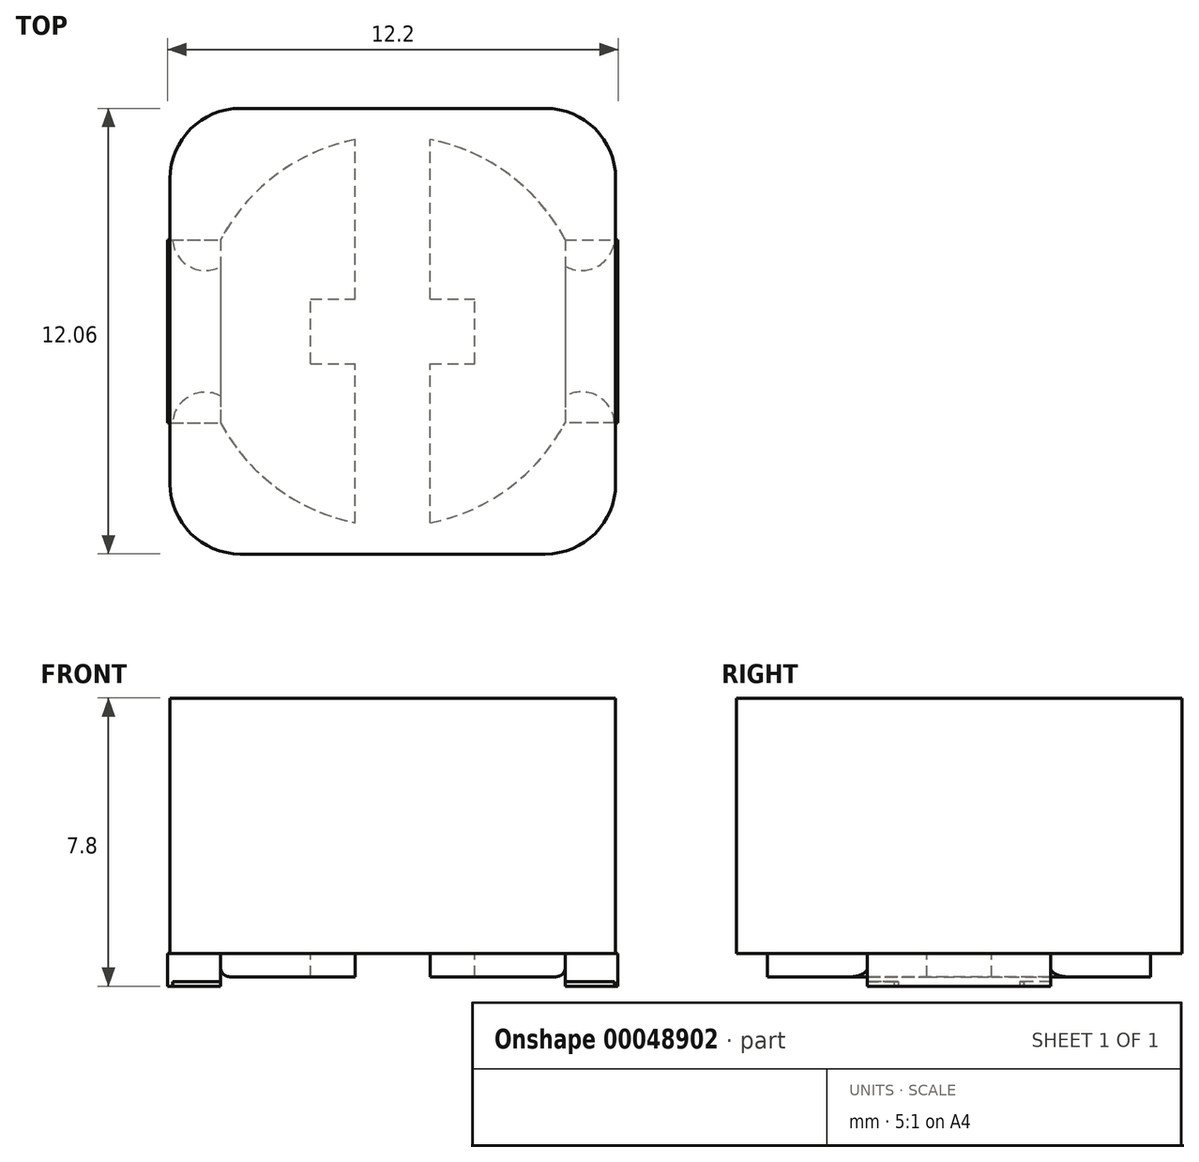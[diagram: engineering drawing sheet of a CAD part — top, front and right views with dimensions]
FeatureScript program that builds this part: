
annotation { "Feature Type Name" : "Feature", "Feature Type Description" : "" }
export const myFeature = defineFeature(function(context is Context, id is Id, definition is map)
    precondition{}
    {
        {
            var Q0;
            Q0=qCreatedBy(makeId("Top.planeOp"),FACE);
            var sketch = newSketch(context, id + "F0", { "sketchPlane" : qUnion([Q0])});
            skLineSegment(sketch, "E0.rect.bottom", {"start": v(-6.03, 6.03) * mm, "end": v(6.03, 6.03) * mm});
            skLineSegment(sketch, "E0.rect.top", {"start": v(-6.03, -6.03) * mm, "end": v(6.03, -6.03) * mm});
            skLineSegment(sketch, "E0.rect.left", {"start": v(-6.03, 6.03) * mm, "end": v(-6.03, -6.03) * mm});
            skLineSegment(sketch, "E0.rect.right", {"start": v(6.03, 6.03) * mm, "end": v(6.03, -6.03) * mm});
            skPoint(sketch, "E0.rect.middle", {"position": v(0, 0) * mm});
            skSolve(sketch);
        }
        {
            var Q0;
            Q0 = qSketchRegion(id + "F0", true);
            extrude(context, id + "F1", {"entities" : qUnion([Q0]), "depth" : 6.9 * mm});
        }
        {
            var Q0;
            Q0=makeQuery(id+"F1.opExtrude","SWEPT_EDGE",EDGE,{"disambiguationData":[OSD([sQuery(id+"F0.wireOp",EDGE,"E0.rect.top"),sQuery(id+"F0.wireOp",EDGE,"E0.rect.left")])]});
            var Q1;
            Q1=makeQuery(id+"F1.opExtrude","SWEPT_EDGE",EDGE,{"disambiguationData":[OSD([sQuery(id+"F0.wireOp",EDGE,"E0.rect.top"),sQuery(id+"F0.wireOp",EDGE,"E0.rect.right")])]});
            var Q2;
            Q2=makeQuery(id+"F1.opExtrude","SWEPT_EDGE",EDGE,{"disambiguationData":[OSD([sQuery(id+"F0.wireOp",EDGE,"E0.rect.bottom"),sQuery(id+"F0.wireOp",EDGE,"E0.rect.left")])]});
            var Q3;
            Q3=makeQuery(id+"F1.opExtrude","SWEPT_EDGE",EDGE,{"disambiguationData":[OSD([sQuery(id+"F0.wireOp",EDGE,"E0.rect.bottom"),sQuery(id+"F0.wireOp",EDGE,"E0.rect.right")])]});
            fillet(context, id + "F2", {"entities" : qUnion([Q0, Q1, Q2, Q3]), "radius" : 1.9 * mm, "tangentPropagation" : true, "allowEdgeOverflow" : false});
        }
        {
            var Q0;
            Q0=qCreatedBy(makeId("Top.planeOp"),FACE);
            var sketch = newSketch(context, id + "F3", { "sketchPlane" : qUnion([Q0])});
            skLineSegment(sketch, "E1.rect.bottom", {"start": v(-6.1, 2.48) * mm, "end": v(-4.67, 2.48) * mm});
            skLineSegment(sketch, "E1.rect.top", {"start": v(-6.1, -2.48) * mm, "end": v(-4.67, -2.48) * mm});
            skLineSegment(sketch, "E1.rect.left", {"start": v(-6.1, 2.48) * mm, "end": v(-6.1, -2.48) * mm});
            skLineSegment(sketch, "E1.rect.right", {"start": v(6.1, 2.48) * mm, "end": v(6.1, -2.48) * mm});
            skPoint(sketch, "E1.rect.middle", {"position": v(0, 0) * mm});
            skArc(sketch, "E2", {"start": v(-4.67, -2.48) * mm, "mid": v(-3.15, -4.24) * mm, "end": v(-1.02, -5.18) * mm});
            skLineSegment(sketch, "E3", {"start": v(-4.67, 2.48) * mm, "end": v(-6.1, 2.48) * mm});
            skLineSegment(sketch, "E4", {"start": v(6.1, -2.48) * mm, "end": v(4.67, -2.48) * mm});
            skLineSegment(sketch, "E5", {"start": v(4.67, 2.48) * mm, "end": v(6.1, 2.48) * mm});
            skArc(sketch, "E6.trimOffspring", {"start": v(4.67, 2.48) * mm, "mid": v(3.15, 4.24) * mm, "end": v(1.02, 5.18) * mm});
            skLineSegment(sketch, "E7.rect.left", {"start": v(-1.02, -5.18) * mm, "end": v(-1.02, 5.18) * mm});
            skLineSegment(sketch, "E7.rect.right", {"start": v(1.02, -5.18) * mm, "end": v(1.02, 5.18) * mm});
            skArc(sketch, "E8.trimOffspring", {"start": v(-1.02, 5.18) * mm, "mid": v(-3.15, 4.24) * mm, "end": v(-4.67, 2.48) * mm});
            skArc(sketch, "E9.trimOffspring", {"start": v(1.02, -5.18) * mm, "mid": v(3.15, -4.24) * mm, "end": v(4.67, -2.48) * mm});
            skLineSegment(sketch, "E10", {"start": v(-4.67, 2.48) * mm, "end": v(-4.67, -2.48) * mm});
            skLineSegment(sketch, "E11", {"start": v(4.67, 2.48) * mm, "end": v(4.67, -2.48) * mm});
            skLineSegment(sketch, "E12.rect.bottom", {"start": v(-2.22, -0.88) * mm, "end": v(2.22, -0.88) * mm});
            skLineSegment(sketch, "E12.rect.top", {"start": v(-2.22, 0.88) * mm, "end": v(2.22, 0.88) * mm});
            skLineSegment(sketch, "E12.rect.left", {"start": v(-2.22, -0.88) * mm, "end": v(-2.22, 0.88) * mm});
            skLineSegment(sketch, "E12.rect.right", {"start": v(2.22, -0.88) * mm, "end": v(2.22, 0.88) * mm});
            skLineSegment(sketch, "E13", {"start": v(-1.02, -0.88) * mm, "end": v(-2.22, -0.88) * mm});
            skLineSegment(sketch, "E14", {"start": v(-2.22, 0.88) * mm, "end": v(-1.02, 0.88) * mm});
            skLineSegment(sketch, "E15", {"start": v(-1.02, 0.88) * mm, "end": v(1.02, -0.88) * mm});
            skLineSegment(sketch, "E16", {"start": v(1.02, -0.88) * mm, "end": v(2.22, -0.88) * mm});
            skLineSegment(sketch, "E17", {"start": v(2.22, 0.88) * mm, "end": v(1.02, 0.88) * mm});
            skSolve(sketch);
        }
        {
            var Q0;
            Q0=makeQuery(id+"F3.imprint","IMPRINT",FACE,{"disambiguationData":[TD([[makeQuery(id+"F3.imprint","IMPRINT",EDGE,{"derivedFrom":sQuery(id+"F3.wireOp",EDGE,"E2")}),1.0]])]});
            var Q1;
            Q1=makeQuery(id+"F3.imprint","IMPRINT",FACE,{"disambiguationData":[TD([[makeQuery(id+"F3.imprint","IMPRINT",EDGE,{"derivedFrom":sQuery(id+"F3.wireOp",EDGE,"E6.trimOffspring")}),1.0]])]});
            extrude(context, id + "F4", {"entities" : qUnion([Q0, Q1]), "oppositeDirection" : true, "depth" : 0.64 * mm});
        }
        {
            var Q0;
            Q0=makeQuery(id+"F3.imprint","IMPRINT",FACE,{"disambiguationData":[TD([[makeQuery(id+"F3.imprint","IMPRINT",EDGE,{"derivedFrom":sQuery(id+"F3.wireOp",EDGE,"E1.rect.right")}),-1.0]])]});
            extrude(context, id + "F5", {"entities" : qUnion([Q0]), "oppositeDirection" : true, "depth" : 0.89 * mm});
        }
        {
            var Q0;
            Q0=makeQuery(id+"F3.imprint","IMPRINT",FACE,{"disambiguationData":[TD([[makeQuery(id+"F3.imprint","IMPRINT",EDGE,{"derivedFrom":sQuery(id+"F3.wireOp",EDGE,"E1.rect.left")}),1.0]])]});
            extrude(context, id + "F6", {"entities" : qUnion([Q0]), "oppositeDirection" : true, "depth" : 0.89 * mm});
        }
        {
            var Q0;
            Q0=makeQuery(id+"F4.opExtrude","CAP_EDGE",EDGE,{"disambiguationData":[OSD([sQuery(id+"F3.wireOp",EDGE,"E11")])],"isStart":false});
            fillet(context, id + "F7", {"entities" : qUnion([Q0]), "radius" : 0.25 * mm, "tangentPropagation" : true, "allowEdgeOverflow" : false});
        }
        {
            var Q0;
            Q0=makeQuery(id+"F4.opExtrude","CAP_EDGE",EDGE,{"disambiguationData":[OSD([sQuery(id+"F3.wireOp",EDGE,"E10")])],"isStart":false});
            fillet(context, id + "F8", {"entities" : qUnion([Q0]), "radius" : 0.25 * mm, "tangentPropagation" : true, "allowEdgeOverflow" : false});
        }
        {
            var Q0;
            Q0=makeQuery(id+"F6.opExtrude","CAP_FACE",FACE,{"disambiguationData":[OSD([sQuery(id+"F3.wireOp",EDGE,"E1.rect.left"),sQuery(id+"F3.wireOp",EDGE,"E1.rect.top"),sQuery(id+"F3.wireOp",EDGE,"E3"),sQuery(id+"F3.wireOp",EDGE,"E10")])],"isStart":false});
            var sketch = newSketch(context, id + "F9", { "sketchPlane" : qUnion([Q0])});
            skCircle(sketch, "E18", {"center": v(-5.08, 2.54) * mm, "radius": 0.89 * mm});
            skCircle(sketch, "E19", {"center": v(5.11, 2.53) * mm, "radius": 0.89 * mm});
            skCircle(sketch, "E20", {"center": v(5.11, -2.53) * mm, "radius": 0.89 * mm});
            skCircle(sketch, "E21", {"center": v(-5.08, -2.53) * mm, "radius": 0.89 * mm});
            skSolve(sketch);
        }
        {
            var Q0;
            {var subQ0=sQuery(id+"F9.wireOp",EDGE,"E18");var subQ1=sQuery(id+"F3.wireOp",EDGE,"E1.rect.top");var subQ2=makeQuery(id+"F6.opExtrude","CAP_EDGE",EDGE,{"disambiguationData":[OSD([subQ1])],"isStart":false});var subQ3=makeQuery(id+"F9.imprint","INTERSECT",VERTEX,{"derivedFrom":[subQ2,subQ0]});Q0=makeQuery(id+"F9.imprint","IMPRINT",FACE,{"disambiguationData":[TD([[makeQuery(id+"F9.imprint","IMPRINT",EDGE,{"disambiguationData":[TD([[subQ3,-1.0]])],"derivedFrom":subQ0}),1.0]])]});}
            var Q1;
            {var subQ0=sQuery(id+"F9.wireOp",EDGE,"E21");var subQ1=sQuery(id+"F3.wireOp",EDGE,"E3");var subQ2=makeQuery(id+"F6.opExtrude","CAP_EDGE",EDGE,{"disambiguationData":[OSD([subQ1])],"isStart":false});var subQ3=makeQuery(id+"F9.imprint","INTERSECT",VERTEX,{"derivedFrom":[subQ2,subQ0]});Q1=makeQuery(id+"F9.imprint","IMPRINT",FACE,{"disambiguationData":[TD([[makeQuery(id+"F9.imprint","IMPRINT",EDGE,{"disambiguationData":[TD([[subQ3,1.0]])],"derivedFrom":subQ0}),1.0]])]});}
            var Q2;
            Q2=makeQuery(id+"F9.imprint","IMPRINT",FACE,{"disambiguationData":[TD([[makeQuery(id+"F9.imprint","IMPRINT",EDGE,{"derivedFrom":sQuery(id+"F9.wireOp",EDGE,"E20")}),1.0]])]});
            var Q3;
            Q3=makeQuery(id+"F9.imprint","IMPRINT",FACE,{"disambiguationData":[TD([[makeQuery(id+"F9.imprint","IMPRINT",EDGE,{"derivedFrom":sQuery(id+"F9.wireOp",EDGE,"E19")}),1.0]])]});
            extrude(context, id + "F10", {"entities" : qUnion([Q0, Q1, Q2, Q3]), "operationType" : NewBodyOperationType.REMOVE, "oppositeDirection" : true, "depth" : 0.13 * mm});
        }
        {
            var Q0;
            Q0=makeQuery(id+"F9.imprint","IMPRINT",FACE,{"disambiguationData":[TD([[makeQuery(id+"F9.imprint","IMPRINT",EDGE,{"derivedFrom":sQuery(id+"F9.wireOp",EDGE,"E19")}),1.0]])]});
            var Q1;
            Q1=makeQuery(id+"F9.imprint","IMPRINT",FACE,{"disambiguationData":[TD([[makeQuery(id+"F9.imprint","IMPRINT",EDGE,{"derivedFrom":sQuery(id+"F9.wireOp",EDGE,"E20")}),1.0]])]});
            extrude(context, id + "F11", {"entities" : qUnion([Q0, Q1]), "operationType" : NewBodyOperationType.REMOVE, "oppositeDirection" : true, "depth" : 0.13 * mm});
        }
    });
